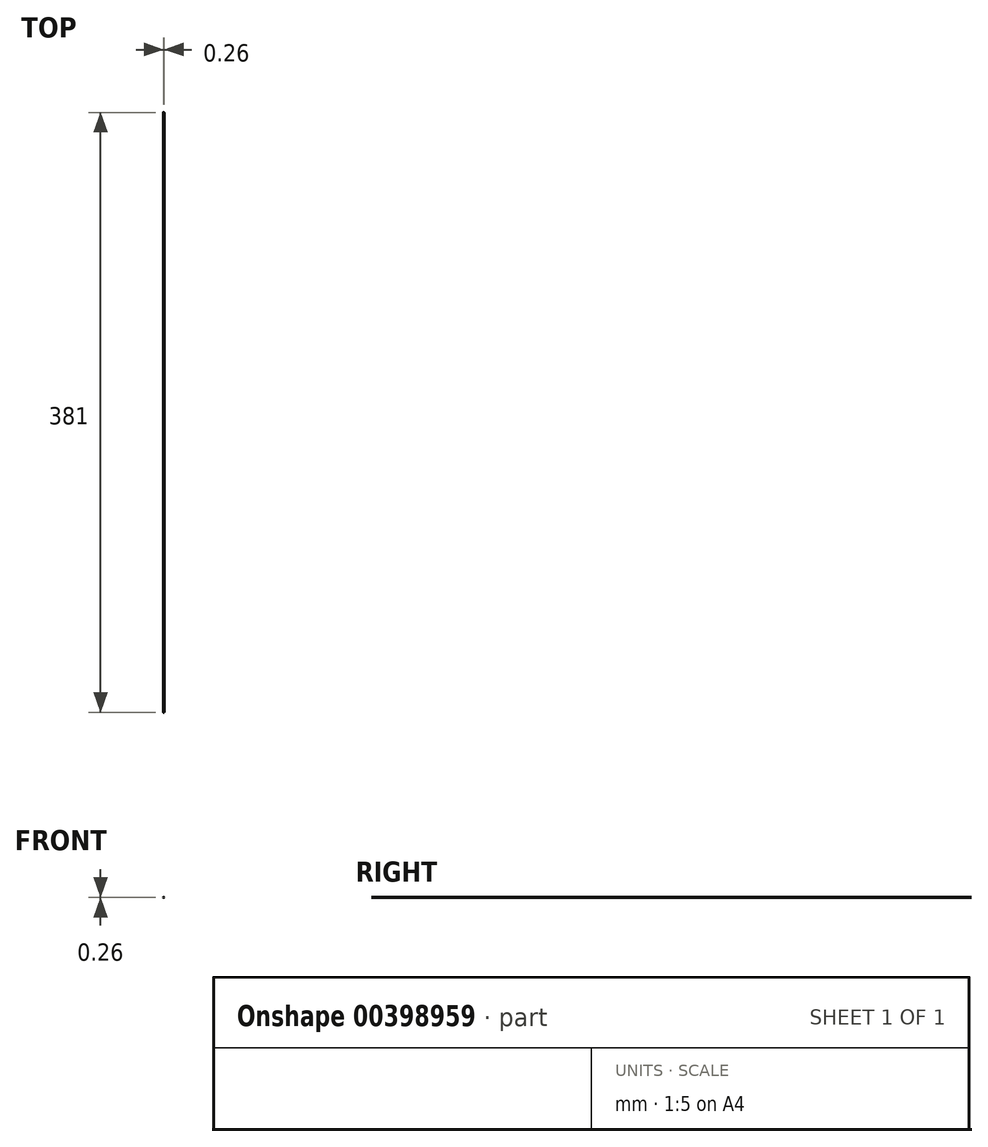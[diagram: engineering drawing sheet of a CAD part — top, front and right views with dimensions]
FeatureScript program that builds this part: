
annotation { "Feature Type Name" : "Feature", "Feature Type Description" : "" }
export const myFeature = defineFeature(function(context is Context, id is Id, definition is map)
    precondition{}
    {
        {
            var Q0;
            Q0=qCreatedBy(makeId("Front.planeOp"),FACE);
            var sketch = newSketch(context, id + "F0", { "sketchPlane" : qUnion([Q0])});
            skCircle(sketch, "E0", {"center": v(0, 0) * mm, "radius": 0.13 * mm});
            skSolve(sketch);
        }
        {
            var Q0;
            Q0 = qSketchRegion(id + "F0", true);
            extrude(context, id + "F1", {"entities" : qUnion([Q0]), "depth" : 381 * mm, "symmetric" : true});
        }
    });
